# Revit family: Practibox_S_flush_mounting_cabinet_12_modules_réf_135001_to_135174
name_source: partatom
category: Equipement électrique
revit_build: Autodesk Revit 2018 (Build: 20170223_1515(x64)
units: mm (PartAtom-declared; Revit-internal decimal feet)

## family parameters
Basée sur le plan de construction = Non
Configuration du panneau = Deux colonnes, circuits au sein
Cote de connecteur circulaire = Utiliser le diamètre
Couper avec des vides une fois chargée = Non
Numéro OmniClass = 23.80.30.11.17
Partagée = Non
Point de calcul de pièce = Non
Titre OmniClass = Distribution Boards and Control Panels
Toujours verticalement = Oui
Type d'élément = Tableau de raccordement

## types (32) — shared parameters
Fabricant = "Legrand"
General Conditions of Use = https://export.legrand.com
URL = www.legrand.com
width = 328 mm  [stored 1.07612 ft]

## per-type parameters (varying)
| type | 1R | 2R | 3R | 4R | Ina | Terminal block E | Terminal block N | depth | door B 1 r | door B 2 r | door B 3 r | door B 4 r | door T 1 r | door T 2 r | door T 3 r | door T 4 r | door transparent | door white | height | size |
| Practibox_S_flush_mounting_cabinet_12_modules_135021 | Oui | Non | Non | Non | 63 A |  |  | 102 mm | Oui | Non | Non | Non | Non | Non | Non | Non | Non | Oui | 235 mm  [stored 0.770997 ft] | 1 row |
| Practibox_S_flush_mounting_cabinet_24_modules_135022 | Non | Oui | Non | Non | 90 A |  |  | 103 mm  [stored 0.337927 ft] | Non | Oui | Non | Non | Non | Non | Non | Non | Non | Oui | 385 mm  [stored 1.26312 ft] | 2 row |
| Practibox_S_flush_mounting_cabinet_36_modules_135023 | Non | Non | Oui | Non | 90 A |  |  | 103 mm  [stored 0.337927 ft] | Non | Non | Oui | Non | Non | Non | Non | Non | Non | Oui | 535 mm  [stored 1.75525 ft] | 3 row |
| Practibox_S_flush_mounting_cabinet_48_modules_135024 | Non | Non | Non | Oui | 90 A |  |  | 103 mm  [stored 0.337927 ft] | Non | Non | Non | Oui | Non | Non | Non | Non | Non | Oui | 765 mm  [stored 2.50984 ft] | 4 row |
| Practibox_S_flush_mounting_cabinet_12_modules_135031 | Oui | Non | Non | Non | 63 A |  |  | 102 mm | Non | Non | Non | Non | Oui | Non | Non | Non | Oui | Non | 235 mm  [stored 0.770997 ft] | 1 row |
| Practibox_S_flush_mounting_cabinet_12_modules_135161 | Oui | Non | Non | Non | 63 A | 24 connections Icc 6kA | 24 connections Icc 6kA | 102 mm | Oui | Non | Non | Non | Non | Non | Non | Non | Non | Oui | 235 mm  [stored 0.770997 ft] | 1 row |
| Practibox_S_flush_mounting_cabinet_12_modules_135171 | Oui | Non | Non | Non | 63 A | 24 connections Icc 6kA | 24 connections Icc 6kA | 102 mm | Non | Non | Non | Non | Oui | Non | Non | Non | Oui | Non | 235 mm  [stored 0.770997 ft] | 1 row |
| Practibox_S_flush_mounting_cabinet_12_modules_135151 | Oui | Non | Non | Non | 63 A | 24 connections Icc 6kA | 24 connections Icc 6kA | 102 mm | Non | Non | Non | Non | Oui | Non | Non | Non | Oui | Non | 235 mm  [stored 0.770997 ft] | 1 row |
| Practibox_S_flush_mounting_cabinet_12_modules_135141 | Oui | Non | Non | Non | 63 A | 24 connections Icc 6kA | 24 connections Icc 6kA | 102 mm | Oui | Non | Non | Non | Non | Non | Non | Non | Non | Oui | 235 mm  [stored 0.770997 ft] | 1 row |
| Practibox_S_flush_mounting_cabinet_24_modules_135032 | Non | Oui | Non | Non | 90 A |  |  | 103 mm  [stored 0.337927 ft] | Non | Non | Non | Non | Non | Oui | Non | Non | Oui | Non | 385 mm  [stored 1.26312 ft] | 2 row |
| Practibox_S_flush_mounting_cabinet_24_modules_135162 | Non | Oui | Non | Non | 90 A | 24 connections Icc 6kA | 24 connections Icc 6kA | 103 mm  [stored 0.337927 ft] | Non | Oui | Non | Non | Non | Non | Non | Non | Non | Oui | 385 mm  [stored 1.26312 ft] | 2 row |
| Practibox_S_flush_mounting_cabinet_24_modules_135172 | Non | Oui | Non | Non | 90 A | 24 connections Icc 6kA | 24 connections Icc 6kA | 103 mm  [stored 0.337927 ft] | Non | Non | Non | Non | Non | Oui | Non | Non | Oui | Non | 385 mm  [stored 1.26312 ft] | 2 row |
| Practibox_S_flush_mounting_cabinet_24_modules_135142 | Non | Oui | Non | Non | 90 A | 24 connections Icc 6kA | 24 connections Icc 6kA | 103 mm  [stored 0.337927 ft] | Non | Oui | Non | Non | Non | Non | Non | Non | Non | Oui | 385 mm  [stored 1.26312 ft] | 2 row |
| Practibox_S_flush_mounting_cabinet_24_modules_135002 | Non | Oui | Non | Non | 90 A |  |  | 103 mm  [stored 0.337927 ft] | Non | Oui | Non | Non | Non | Non | Non | Non | Non | Oui | 385 mm  [stored 1.26312 ft] | 2 row |
| Practibox_S_flush_mounting_cabinet_24_modules_135012 | Non | Oui | Non | Non | 90 A |  |  | 103 mm  [stored 0.337927 ft] | Non | Non | Non | Non | Non | Oui | Non | Non | Oui | Non | 385 mm  [stored 1.26312 ft] | 2 row |
| Practibox_S_flush_mounting_cabinet_36_modules_135033 | Non | Non | Oui | Non | 90 A |  |  | 103 mm  [stored 0.337927 ft] | Non | Non | Non | Non | Non | Non | Oui | Non | Oui | Non | 535 mm  [stored 1.75525 ft] | 3 row |
| Practibox_S_flush_mounting_cabinet_36_modules_135173 | Non | Non | Oui | Non | 90 A | 24 connections Icc 6kA | 24 connections Icc 6kA | 103 mm  [stored 0.337927 ft] | Non | Non | Non | Non | Non | Non | Oui | Non | Oui | Non | 535 mm  [stored 1.75525 ft] | 3 row |
| Practibox_S_flush_mounting_cabinet_36_modules_135163 | Non | Non | Oui | Non | 90 A | 24 connections Icc 6kA | 24 connections Icc 6kA | 103 mm  [stored 0.337927 ft] | Non | Non | Oui | Non | Non | Non | Non | Non | Non | Oui | 535 mm  [stored 1.75525 ft] | 3 row |
| Practibox_S_flush_mounting_cabinet_36_modules_135143 | Non | Non | Oui | Non | 90 A | 24 connections Icc 6kA | 24 connections Icc 6kA | 103 mm  [stored 0.337927 ft] | Non | Non | Oui | Non | Non | Non | Non | Non | Non | Oui | 535 mm  [stored 1.75525 ft] | 3 row |
| Practibox_S_flush_mounting_cabinet_36_modules_135153 | Non | Non | Oui | Non | 90 A | 24 connections Icc 6kA | 24 connections Icc 6kA | 103 mm  [stored 0.337927 ft] | Non | Non | Non | Non | Non | Non | Oui | Non | Oui | Non | 535 mm  [stored 1.75525 ft] | 3 row |
| Practibox_S_flush_mounting_cabinet_36_modules_135013 | Non | Non | Oui | Non | 90 A |  |  | 103 mm  [stored 0.337927 ft] | Non | Non | Non | Non | Non | Non | Oui | Non | Oui | Non | 535 mm  [stored 1.75525 ft] | 3 row |
| Practibox_S_flush_mounting_cabinet_36_modules_135003 | Non | Non | Oui | Non | 90 A |  |  | 103 mm  [stored 0.337927 ft] | Non | Non | Oui | Non | Non | Non | Non | Non | Non | Oui | 535 mm  [stored 1.75525 ft] | 3 row |
| Practibox_S_flush_mounting_cabinet_48_modules_135034 | Non | Non | Non | Oui | 90 A |  |  | 103 mm  [stored 0.337927 ft] | Non | Non | Non | Non | Non | Non | Non | Oui | Oui | Non | 765 mm  [stored 2.50984 ft] | 4 row |
| Practibox_S_flush_mounting_cabinet_48_modules_135174 | Non | Non | Non | Oui | 90 A | 24 connections Icc 6kA | 24 connections Icc 6kA | 103 mm  [stored 0.337927 ft] | Non | Non | Non | Non | Non | Non | Non | Oui | Oui | Non | 765 mm  [stored 2.50984 ft] | 4 row |
| Practibox_S_flush_mounting_cabinet_48_modules_135164 | Non | Non | Non | Oui | 90 A | 24 connections Icc 6kA | 24 connections Icc 6kA | 103 mm  [stored 0.337927 ft] | Non | Non | Non | Oui | Non | Non | Non | Non | Non | Oui | 765 mm  [stored 2.50984 ft] | 4 row |
| Practibox_S_flush_mounting_cabinet_48_modules_135144 | Non | Non | Non | Oui | 90 A | 24 connections Icc 6kA | 24 connections Icc 6kA | 103 mm  [stored 0.337927 ft] | Non | Non | Non | Oui | Non | Non | Non | Non | Non | Oui | 765 mm  [stored 2.50984 ft] | 4 row |
| Practibox_S_flush_mounting_cabinet_48_modules_135154 | Non | Non | Non | Oui | 90 A | 24 connections Icc 6kA | 24 connections Icc 6kA | 103 mm  [stored 0.337927 ft] | Non | Non | Non | Non | Non | Non | Non | Oui | Oui | Non | 765 mm  [stored 2.50984 ft] | 4 row |
| Practibox_S_flush_mounting_cabinet_48_modules_135004 | Non | Non | Non | Oui | 90 A |  |  | 103 mm  [stored 0.337927 ft] | Non | Non | Non | Oui | Non | Non | Non | Non | Non | Oui | 765 mm  [stored 2.50984 ft] | 4 row |
| Practibox_S_flush_mounting_cabinet_48_modules_135014 | Non | Non | Non | Oui | 90 A |  |  | 103 mm  [stored 0.337927 ft] | Non | Non | Non | Non | Non | Non | Non | Oui | Oui | Non | 765 mm  [stored 2.50984 ft] | 4 row |
| Practibox_S_flush_mounting_cabinet_24_modules_135152 | Non | Oui | Non | Non | 90 A | 24 connections Icc 6kA | 24 connections Icc 6kA | 103 mm  [stored 0.337927 ft] | Non | Non | Non | Non | Non | Oui | Non | Non | Oui | Non | 385 mm  [stored 1.26312 ft] | 2 row |
| Practibox_S_flush_mounting_cabinet_12_modules_135001 | Oui | Non | Non | Non | 63 A |  |  | 102 mm | Oui | Non | Non | Non | Non | Non | Non | Non | Non | Oui | 235 mm  [stored 0.770997 ft] | 1 row |
| Practibox_S_flush_mounting_cabinet_12_modules_135011 | Oui | Non | Non | Non | 63 A |  |  | 102 mm | Non | Non | Non | Non | Oui | Non | Non | Non | Oui | Non | 235 mm  [stored 0.770997 ft] | 1 row |

note: column(s) folded — value = type name in every type: Description

note: [stored X ft] marks values corroborated as IEEE doubles in the binary element streams (Revit-internal decimal feet)
